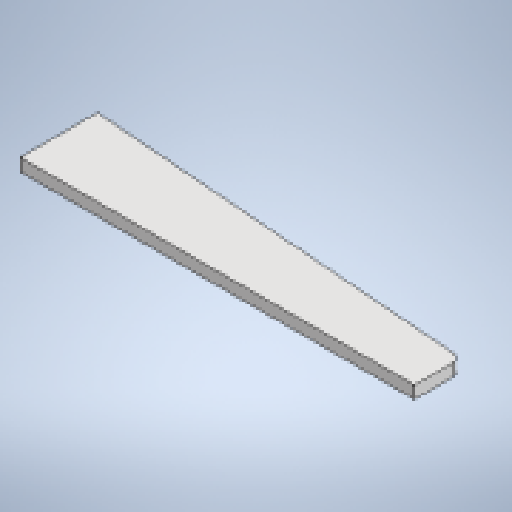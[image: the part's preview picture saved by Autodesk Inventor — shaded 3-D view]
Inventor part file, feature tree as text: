
AUTODESK INVENTOR PART (.ipt)
format: ipt  version: 2025.1 (Build 291241020, 241B)  size: 164,864 bytes
history: native  units: mm
features: other x2, sheet_metal_op x1, chamfer x1, sketch x1
ambient origin geometry x8: Origin, YZ Plane, XZ Plane, XY Plane, X Axis, Y Axis, Z Axis, Center Point
bodies: Body1 (feature_tree)
feature tree (5):
  sheet_metal_op  "Face1"
  chamfer  "Corner Round1"
  sketch  "Sketch3"  dims[d11=300.0mm d12=30.0mm d13=45.0mm d14=50.0mm d15=8.0mm d16=6.0mm]
  other  "Plate1"
  other  "Definition1"
